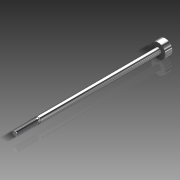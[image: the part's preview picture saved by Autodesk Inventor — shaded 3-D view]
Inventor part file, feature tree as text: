
AUTODESK INVENTOR PART (.ipt)
format: ipt  version: 2014 SP1 (Build 180222100, 222)  size: 89,600 bytes
history: native  units: in
note: dims shown in document units (in); Inventor stores cm internally (conversion verified against a paired STEP export)
features: other x1, imported_body x1, thread x1
ambient origin geometry x8: Origin, YZ Plane, XZ Plane, XY Plane, X Axis, Y Axis, Z Axis, Center Point
bodies: Body1 (feature_tree)
feature tree (3):
  parser-record x1  (decoder bookkeeping rows leaked as tree rows — omitted from the tree; the rows remain in map.json)
  imported_body  "Base1"
  thread  "Thread1"  [1 undecoded]
note: 1 required parameter value undecoded (feature->parameter linkage not recoverable at this tier; creation-order binding heuristic only, values carry confidence <= 0.55)
